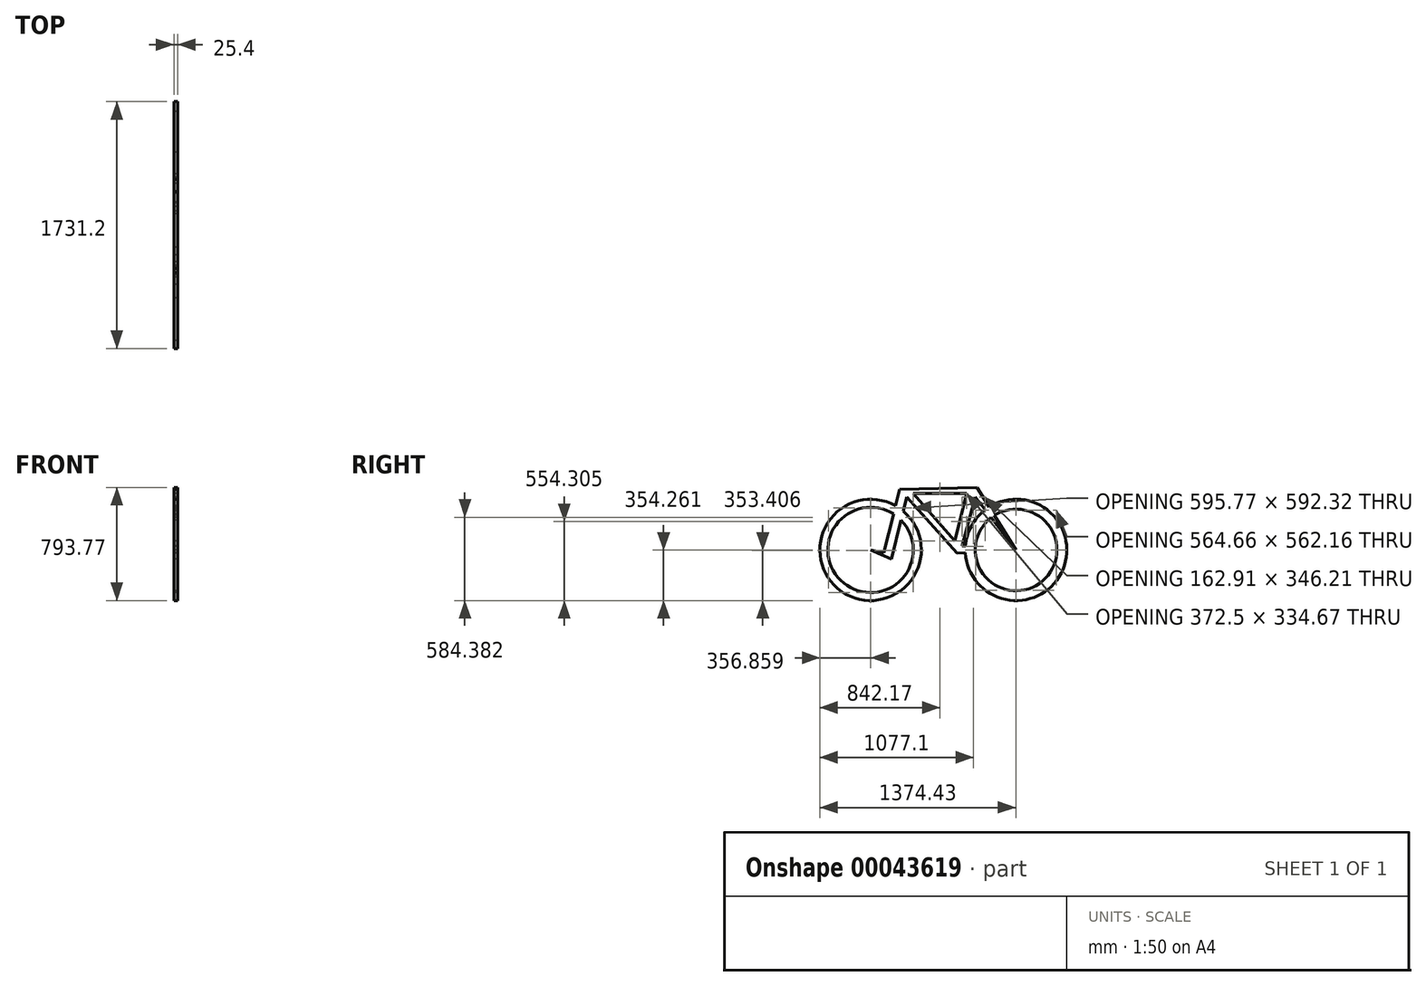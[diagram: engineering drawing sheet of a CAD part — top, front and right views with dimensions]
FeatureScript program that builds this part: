
annotation { "Feature Type Name" : "Feature", "Feature Type Description" : "" }
export const myFeature = defineFeature(function(context is Context, id is Id, definition is map)
    precondition{}
    {
        {
            var Q0;
            Q0=qCreatedBy(makeId("Right.planeOp"),FACE);
            var sketch = newSketch(context, id + "F0", { "sketchPlane" : qUnion([Q0])});
            skCircle(sketch, "E0", {"center": v(-510, 0) * mm, "radius": 355.6 * mm});
            skCircle(sketch, "E1", {"center": v(510, 0) * mm, "radius": 355.6 * mm});
            skLineSegment(sketch, "E2", {"start": v(510, 0) * mm, "end": v(236.66, 438.17) * mm});
            skLineSegment(sketch, "E3", {"start": v(236.66, 438.17) * mm, "end": v(-305.25, 423.52) * mm});
            skLineSegment(sketch, "E4", {"start": v(-305.25, 423.52) * mm, "end": v(-416.98, -19.55) * mm});
            skLineSegment(sketch, "E5", {"start": v(-416.98, -19.55) * mm, "end": v(-510, 0) * mm});
            skLineSegment(sketch, "E6", {"start": v(510, 0) * mm, "end": v(223.51, 371.8) * mm});
            skLineSegment(sketch, "E7", {"start": v(223.51, 371.8) * mm, "end": v(130.04, 27.42) * mm});
            skLineSegment(sketch, "E8", {"start": v(130.04, 27.42) * mm, "end": v(510, 0) * mm});
            skLineSegment(sketch, "E9", {"start": v(510, 0) * mm, "end": v(97.32, -23.55) * mm});
            skLineSegment(sketch, "E10", {"start": v(97.32, -23.55) * mm, "end": v(-305.25, 423.52) * mm});
            skLineSegment(sketch, "E11", {"start": v(-257.02, 369.96) * mm, "end": v(-364.15, -64.6) * mm});
            skLineSegment(sketch, "E12", {"start": v(-364.15, -64.6) * mm, "end": v(-510, 0) * mm});
            skLineSegment(sketch, "E13", {"start": v(-209.68, 396.12) * mm, "end": v(162.82, 396.12) * mm});
            skLineSegment(sketch, "E14", {"start": v(162.82, 396.12) * mm, "end": v(79.3, 61.45) * mm});
            skLineSegment(sketch, "E15", {"start": v(79.3, 61.45) * mm, "end": v(-209.68, 396.12) * mm});
            skCircle(sketch, "E16", {"center": v(-510, 0) * mm, "radius": 299.2 * mm});
            skCircle(sketch, "E17", {"center": v(510, 0) * mm, "radius": 286.35 * mm});
            skSolve(sketch);
        }
        {
            var Q0;
            {var subQ0=sQuery(id+"F0.wireOp",EDGE,"E4");var subQ1=sQuery(id+"F0.wireOp",EDGE,"E0");var subQ2=makeQuery(id+"F0.imprint","INTERSECT",VERTEX,{"derivedFrom":[subQ1,subQ0]});Q0=makeQuery(id+"F0.imprint","IMPRINT",FACE,{"disambiguationData":[TD([[makeQuery(id+"F0.imprint","IMPRINT",EDGE,{"disambiguationData":[TD([[subQ2,-1.0]])],"derivedFrom":subQ1}),1.0]])]});}
            var Q1;
            {var subQ0=sQuery(id+"F0.wireOp",EDGE,"E2");var subQ1=sQuery(id+"F0.wireOp",EDGE,"E1");var subQ2=makeQuery(id+"F0.imprint","INTERSECT",VERTEX,{"derivedFrom":[subQ1,subQ0]});Q1=makeQuery(id+"F0.imprint","IMPRINT",FACE,{"disambiguationData":[TD([[makeQuery(id+"F0.imprint","IMPRINT",EDGE,{"disambiguationData":[TD([[subQ2,1.0]])],"derivedFrom":subQ1}),1.0]])]});}
            var Q2;
            {var subQ1=sQuery(id+"F0.wireOp",EDGE,"E2");var subQ3=sQuery(id+"F0.wireOp",EDGE,"E17");var subQ4=makeQuery(id+"F0.imprint","INTERSECT",VERTEX,{"derivedFrom":[subQ1,subQ3]});Q2=makeQuery(id+"F0.imprint","IMPRINT",FACE,{"disambiguationData":[TD([[makeQuery(id+"F0.imprint","IMPRINT",EDGE,{"disambiguationData":[TD([[subQ4,-1.0]])],"derivedFrom":subQ3}),1.0]])]});}
            var Q3;
            {var subQ0=sQuery(id+"F0.wireOp",EDGE,"E9");var subQ1=sQuery(id+"F0.wireOp",EDGE,"E1");var subQ2=makeQuery(id+"F0.imprint","INTERSECT",VERTEX,{"derivedFrom":[subQ1,subQ0]});Q3=makeQuery(id+"F0.imprint","IMPRINT",FACE,{"disambiguationData":[TD([[makeQuery(id+"F0.imprint","IMPRINT",EDGE,{"disambiguationData":[TD([[subQ2,1.0]])],"derivedFrom":subQ1}),1.0]])]});}
            var Q4;
            {var subQ0=sQuery(id+"F0.wireOp",EDGE,"E6");var subQ1=sQuery(id+"F0.wireOp",EDGE,"E1");var subQ2=makeQuery(id+"F0.imprint","INTERSECT",VERTEX,{"derivedFrom":[subQ1,subQ0]});Q4=makeQuery(id+"F0.imprint","IMPRINT",FACE,{"disambiguationData":[TD([[makeQuery(id+"F0.imprint","IMPRINT",EDGE,{"disambiguationData":[TD([[subQ2,-1.0]])],"derivedFrom":subQ1}),1.0]])]});}
            var Q5;
            {var subQ0=sQuery(id+"F0.wireOp",EDGE,"E2");var subQ1=sQuery(id+"F0.wireOp",EDGE,"E1");var subQ2=makeQuery(id+"F0.imprint","INTERSECT",VERTEX,{"derivedFrom":[subQ1,subQ0]});Q5=makeQuery(id+"F0.imprint","IMPRINT",FACE,{"disambiguationData":[TD([[makeQuery(id+"F0.imprint","IMPRINT",EDGE,{"disambiguationData":[TD([[subQ2,-1.0]])],"derivedFrom":subQ1}),1.0]])]});}
            var Q6;
            {var subQ0=sQuery(id+"F0.wireOp",EDGE,"E4");var subQ1=sQuery(id+"F0.wireOp",EDGE,"E0");var subQ2=makeQuery(id+"F0.imprint","INTERSECT",VERTEX,{"derivedFrom":[subQ1,subQ0]});Q6=makeQuery(id+"F0.imprint","IMPRINT",FACE,{"disambiguationData":[TD([[makeQuery(id+"F0.imprint","IMPRINT",EDGE,{"disambiguationData":[TD([[subQ2,1.0]])],"derivedFrom":subQ1}),1.0]])]});}
            var Q7;
            {var subQ0=sQuery(id+"F0.wireOp",EDGE,"E4");var subQ1=sQuery(id+"F0.wireOp",EDGE,"E0");var subQ2=makeQuery(id+"F0.imprint","INTERSECT",VERTEX,{"derivedFrom":[subQ1,subQ0]});Q7=makeQuery(id+"F0.imprint","IMPRINT",FACE,{"disambiguationData":[TD([[makeQuery(id+"F0.imprint","IMPRINT",EDGE,{"disambiguationData":[TD([[subQ2,1.0]])],"derivedFrom":subQ1}),-1.0]])]});}
            var Q8;
            {var subQ7=sQuery(id+"F0.wireOp",EDGE,"E3");Q8=makeQuery(id+"F0.imprint","IMPRINT",FACE,{"disambiguationData":[TD([[makeQuery(id+"F0.imprint","IMPRINT",EDGE,{"derivedFrom":subQ7}),1.0]])]});}
            var Q9;
            {var subQ6=sQuery(id+"F0.wireOp",EDGE,"E5");Q9=makeQuery(id+"F0.imprint","IMPRINT",FACE,{"disambiguationData":[TD([[makeQuery(id+"F0.imprint","IMPRINT",EDGE,{"derivedFrom":subQ6}),1.0]])]});}
            extrude(context, id + "F1", {"entities" : qUnion([Q0, Q1, Q2, Q3, Q4, Q5, Q6, Q7, Q8, Q9]), "endBound" : BoundingType.SYMMETRIC, "depth" : 25.4 * mm});
        }
    });
